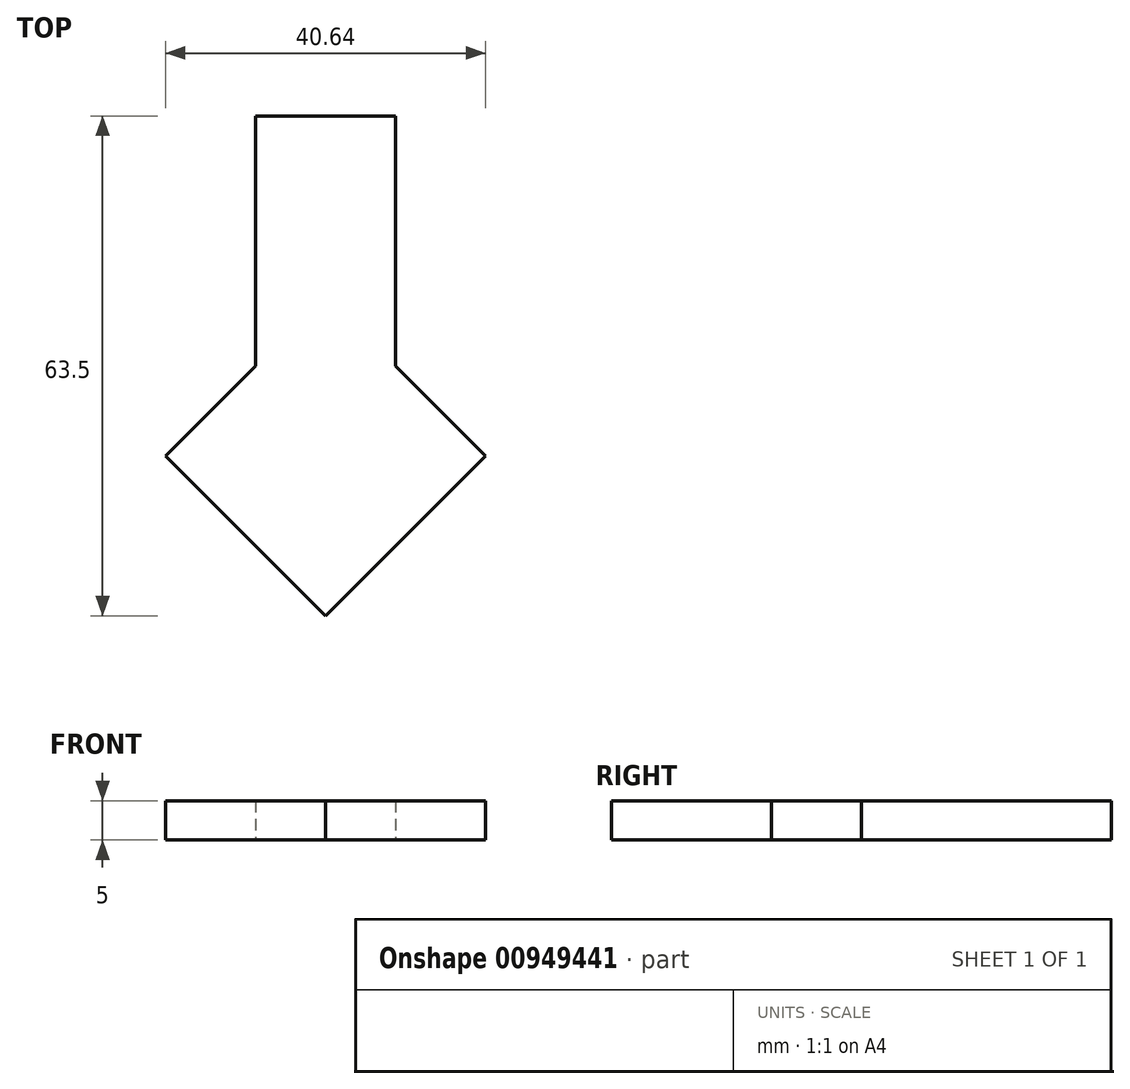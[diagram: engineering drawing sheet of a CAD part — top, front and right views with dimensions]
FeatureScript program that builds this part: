
annotation { "Feature Type Name" : "Feature", "Feature Type Description" : "" }
export const myFeature = defineFeature(function(context is Context, id is Id, definition is map)
    precondition{}
    {
        {
            var Q0;
            Q0=qCreatedBy(makeId("Top.planeOp"),FACE);
            var sketch = newSketch(context, id + "F0", { "sketchPlane" : qUnion([Q0])});
            skLineSegment(sketch, "E0.bottom", {"start": v(-17.78, 22.86) * mm, "end": v(0, 22.86) * mm});
            skLineSegment(sketch, "E0.top", {"start": v(-17.78, 0) * mm, "end": v(0, 0) * mm});
            skLineSegment(sketch, "E0.left", {"start": v(-17.78, 22.86) * mm, "end": v(-17.78, 0) * mm});
            skLineSegment(sketch, "E0.right", {"start": v(0, 22.86) * mm, "end": v(0, 0) * mm});
            skLineSegment(sketch, "E1", {"start": v(-8.89, 0) * mm, "end": v(-8.89, -40.64) * mm, "construction": true});
            skPoint(sketch, "E2", {"position": v(-8.89, -20.32) * mm});
            skLineSegment(sketch, "E3", {"start": v(-8.89, -20.32) * mm, "end": v(11.43, -20.32) * mm, "construction": true});
            skLineSegment(sketch, "E4", {"start": v(-8.89, -20.32) * mm, "end": v(-29.21, -20.32) * mm, "construction": true});
            skLineSegment(sketch, "E5", {"start": v(-29.21, -20.32) * mm, "end": v(-8.89, -40.64) * mm});
            skLineSegment(sketch, "E6", {"start": v(-8.89, -40.64) * mm, "end": v(11.43, -20.32) * mm});
            skLineSegment(sketch, "E7", {"start": v(11.43, -20.32) * mm, "end": v(-8.9, 0) * mm});
            skLineSegment(sketch, "E8", {"start": v(-29.21, -20.32) * mm, "end": v(-8.89, 0) * mm});
            skLineSegment(sketch, "E9", {"start": v(0, 0) * mm, "end": v(0, -8.89) * mm});
            skLineSegment(sketch, "E10", {"start": v(-17.78, 0) * mm, "end": v(-17.78, -8.9) * mm});
            skSolve(sketch);
        }
        {
            var Q0;
            Q0=makeQuery(id+"F0.imprint","IMPRINT",FACE,{"disambiguationData":[TD([[makeQuery(id+"F0.imprint","IMPRINT",EDGE,{"derivedFrom":sQuery(id+"F0.wireOp",EDGE,"E0.bottom")}),-1.0]])]});
            var Q1;
            {var subQ0=sQuery(id+"F0.wireOp",EDGE,"E9");Q1=makeQuery(id+"F0.imprint","IMPRINT",FACE,{"disambiguationData":[TD([[makeQuery(id+"F0.imprint","IMPRINT",EDGE,{"derivedFrom":subQ0}),-1.0]])]});}
            var Q2;
            {var subQ0=sQuery(id+"F0.wireOp",EDGE,"E10");Q2=makeQuery(id+"F0.imprint","IMPRINT",FACE,{"disambiguationData":[TD([[makeQuery(id+"F0.imprint","IMPRINT",EDGE,{"derivedFrom":subQ0}),1.0]])]});}
            var Q3;
            {var subQ5=sQuery(id+"F0.wireOp",EDGE,"E5");Q3=makeQuery(id+"F0.imprint","IMPRINT",FACE,{"disambiguationData":[TD([[makeQuery(id+"F0.imprint","IMPRINT",EDGE,{"derivedFrom":subQ5}),1.0]])]});}
            extrude(context, id + "F1", {"entities" : qUnion([Q0, Q1, Q2, Q3]), "depth" : 5 * mm, "offsetDistance" : 25 * mm});
        }
    });
